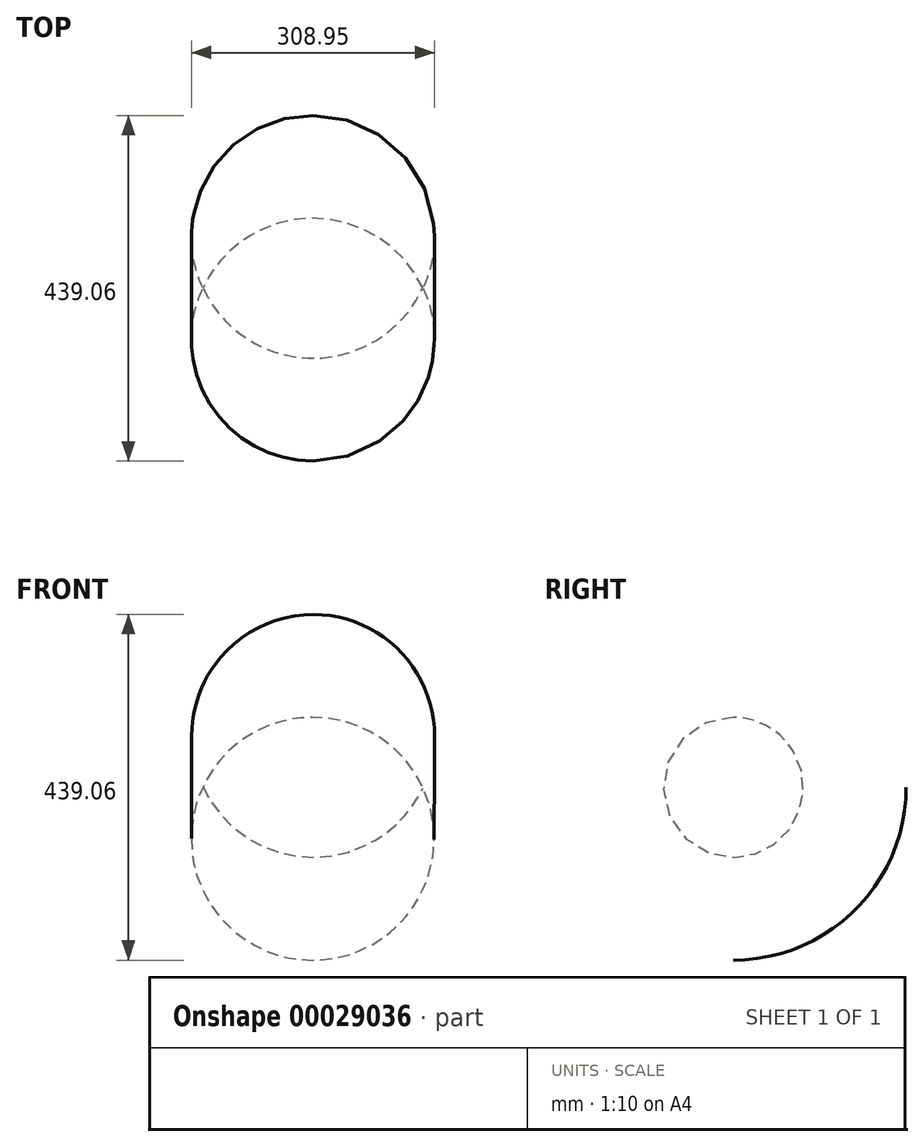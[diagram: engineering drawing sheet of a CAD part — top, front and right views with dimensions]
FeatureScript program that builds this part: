
annotation { "Feature Type Name" : "Feature", "Feature Type Description" : "" }
export const myFeature = defineFeature(function(context is Context, id is Id, definition is map)
    precondition{}
    {
        {
            var Q0;
            Q0=qCreatedBy(makeId("Front.planeOp"),FACE);
            var sketch = newSketch(context, id + "F0", { "sketchPlane" : qUnion([Q0])});
            skArc(sketch, "E0", {"start": v(279.4, 96.11) * mm, "mid": v(140.05, 185.57) * mm, "end": v(0, 97.23) * mm});
            skLineSegment(sketch, "E1", {"start": v(279.4, 96.11) * mm, "end": v(0, 97.23) * mm});
            skSolve(sketch);
        }
        {
            var Q0;
            Q0=makeQuery(id+"F0.imprint","IMPRINT",FACE,{"disambiguationData":[TD([[makeQuery(id+"F0.imprint","IMPRINT",EDGE,{"derivedFrom":sQuery(id+"F0.wireOp",EDGE,"E0")}),1.0]])]});
            var Q1;
            Q1=sQuery(id+"F0.wireOp",EDGE,"E1");
            revolve(context, id + "F1", {"entities" : qUnion([Q0]), "axis" : qUnion([Q1]), "revolveType" : RevolveType.FULL});
        }
    });
